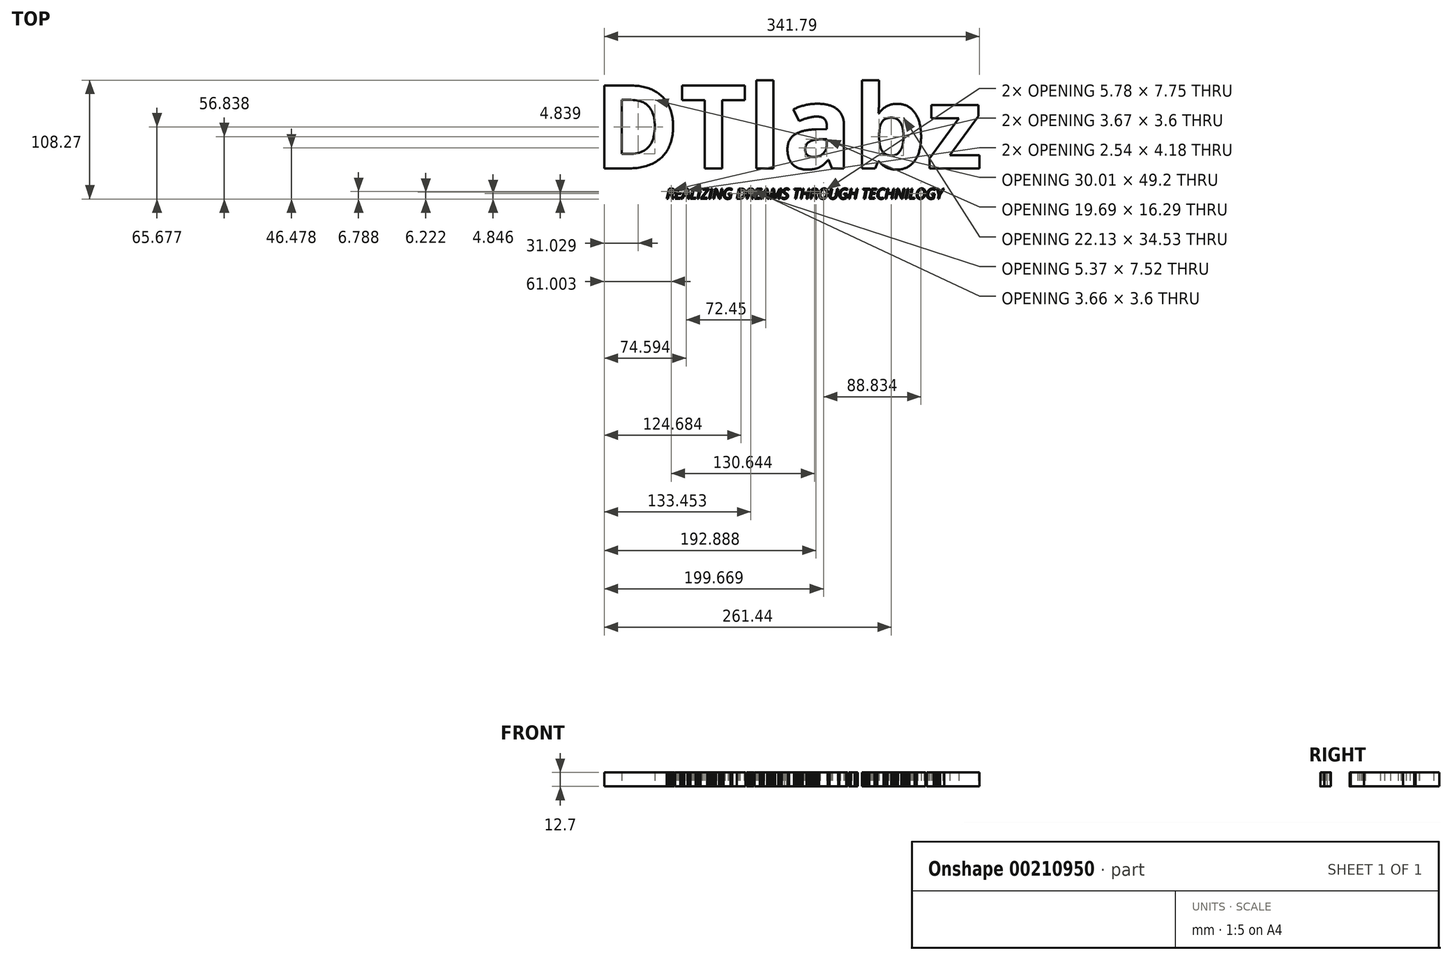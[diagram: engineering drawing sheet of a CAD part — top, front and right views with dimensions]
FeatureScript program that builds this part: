
annotation { "Feature Type Name" : "Feature", "Feature Type Description" : "" }
export const myFeature = defineFeature(function(context is Context, id is Id, definition is map)
    precondition{}
    {
        {
            var Q0;
            Q0=qCreatedBy(makeId("Top.planeOp"),FACE);
            var sketch = newSketch(context, id + "F0", { "sketchPlane" : qUnion([Q0])});
            skText(sketch, "E0", { "text": "DTlabz", "fontName": "OpenSans-Bold.ttf"});
            skText(sketch, "E1", { "text": "REALIZING DREAMS THROUGH TECHNILOGY", "fontName": "OpenSans-Italic.ttf"});
            const initialGuessF0  = {"E0": [-0.19503, -0.00948, 1, 0, 0.0762], "E1": [-0.12903, -0.0372, 1, 0, 0.0095]};
            skSetInitialGuess(sketch, initialGuessF0);
            skSolve(sketch);
        }
        {
            var Q0;
            Q0 = qSketchRegion(id + "F0", true);
            extrude(context, id + "F1", {"entities" : qUnion([Q0]), "depth" : 12.7 * mm});
        }
    });
